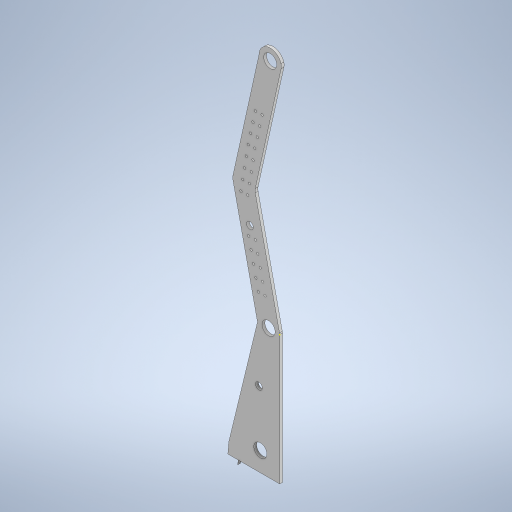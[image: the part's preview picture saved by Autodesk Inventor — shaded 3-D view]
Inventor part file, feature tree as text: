
AUTODESK INVENTOR PART (.ipt)
format: ipt  version: 2023 (Build 270158000, 158)  size: 530,944 bytes
history: native  units: in
note: dims shown in document units (in); Inventor stores cm internally (conversion verified against a paired STEP export)
features: sketch x16, extrude x14, fillet x1, projected_geometry x1
ambient origin geometry x8: Origin, YZ Plane, XZ Plane, XY Plane, X Axis, Y Axis, Z Axis, Center Point
bodies: Body1 (feature_tree), Body2 (feature_tree), Body3 (feature_tree)
feature tree (32):
  extrude  "Extrusion3"  Depth=0.7043in
  sketch  "Sketch3"  dims[d0=4.5in d1=0.7043in]
  extrude  "Extrusion14"  Depth=1.0651in
  extrude  "Extrusion15"  Depth=1.0in
  extrude  "Extrusion16"  Depth=0.5in
  extrude  "Extrusion17"  Depth=0.5in
  extrude  "Extrusion18"  Depth=0.5in
  extrude  "Extrusion19"  Depth=1.0in
  extrude  "Extrusion20"  Depth=0.5in
  sketch  "Sketch11"  dims[d25=0.5325in d26=1.0in]
  sketch  "Sketch12"  dims[d27=1.0in d28=0.5in d29=0.5in]
  fillet  "Fillet1"  Radius=0.5in
  sketch  "Sketch13"  dims[d30=0.25in d31=0.0in d42=1.0in]
  sketch  "Sketch33"  dims[d50=1.5in d51=0.25in]
  extrude  "Extrusion43"  Depth=1.0in
  extrude  "Extrusion44"  Depth=0.25in
  extrude  "Extrusion45"  Depth=0.585in
  extrude  "Extrusion46"  Depth=1.0in TaperAngle=0.0deg
  sketch  "Sketch41"  dims[d91=0.5in]
  extrude  "Extrusion48"  Depth=1.0in TaperAngle=0.0deg
  extrude  "Extrusion49"  Depth=1.0in
  sketch  "Sketch6"  dims[d2=4.5in d3=1.0651in]
  sketch  "Sketch7"  dims[d4=1.0in d5=1.0in]
  sketch  "Sketch8"  dims[d6=1.0in d7=0.5in]
  projected_geometry  "Projected Loop1"
  sketch  "Sketch9"  dims[d8=0.5in d9=0.5in]
  sketch  "Sketch10"  dims[d10=0.5in d24=5.5in]
  sketch  "Sketch37"  dims[d59=0.3in d76=0.585in]
  sketch  "Sketch38"  dims[d77=0.585in d78=1.0in d79=0.0in]
  sketch  "Sketch39"  dims[d82=0.1in d83=1.0in d84=0.0in]
  sketch  "Sketch40"  dims[d89=1.0in d90=0.5325in]
  sketch  "Sketch42"  dims[d92=0.5in d93=0.5in d94=0.5in d95=0.1in d96=0.1in d97=0.1in d98=0.1in d99=0.1in d100=1.0in d101=0.0in d102=0.6in d103=0.1in d104=1.0in d105=0.0in d106=0.125in d107=0.0in d108=2.0in d109=0.3in d110=0.3in d111=0.3in d112=0.3in d113=0.3in d114=0.3in d115=0.3in d116=0.1in d117=0.1in d118=0.1in d119=0.1in d120=0.1in d121=0.1in d122=0.1in d123=0.5in d124=0.5in d125=0.5in d126=0.5in d127=0.5325in d128=0.5in d129=0.5in d130=0.3in d131=0.3in d132=0.3in d133=0.3in d134=0.3in d135=0.3in d136=0.3in d137=0.1in d138=0.1in d139=0.1in d140=0.1in d141=0.1in d142=0.1in d143=0.1in d144=0.1in d145=0.1in d146=0.1in d147=0.1in d148=0.1in d149=0.1in d150=0.1in d151=0.125in d152=0.0in d153=0.125in d154=0.0in d155=0.4in d240=6.0in d241=1.0in d242=0.125in d243=0.0in d244=0.125in d245=0.0in d246=0.2in d247=0.5in d248=0.125in d249=0.0in d250=0.5in d251=0.125in d252=0.0in d253=0.5in d257=0.5in d258=0.125in d259=0.0in d260=2.5in d261=0.6871in d262=0.3in d263=0.125in d264=0.0in d265=0.3in d266=0.1718in d267=0.585in d60=0.0344in d61=0.5in d62=0.0344in d74=0.5in d75=0.0344in d80=0.5in d81=0.0344in d158=0.5in d159=0.0344in d160=0.5in d161=0.0344in d162=0.5in d163=0.0344in d164=0.5in d165=0.0344in d202=0.5in d203=0.0344in d204=0.5in d205=0.0344in d229=0.5in d230=0.0344in d231=0.5in d232=0.0344in]
